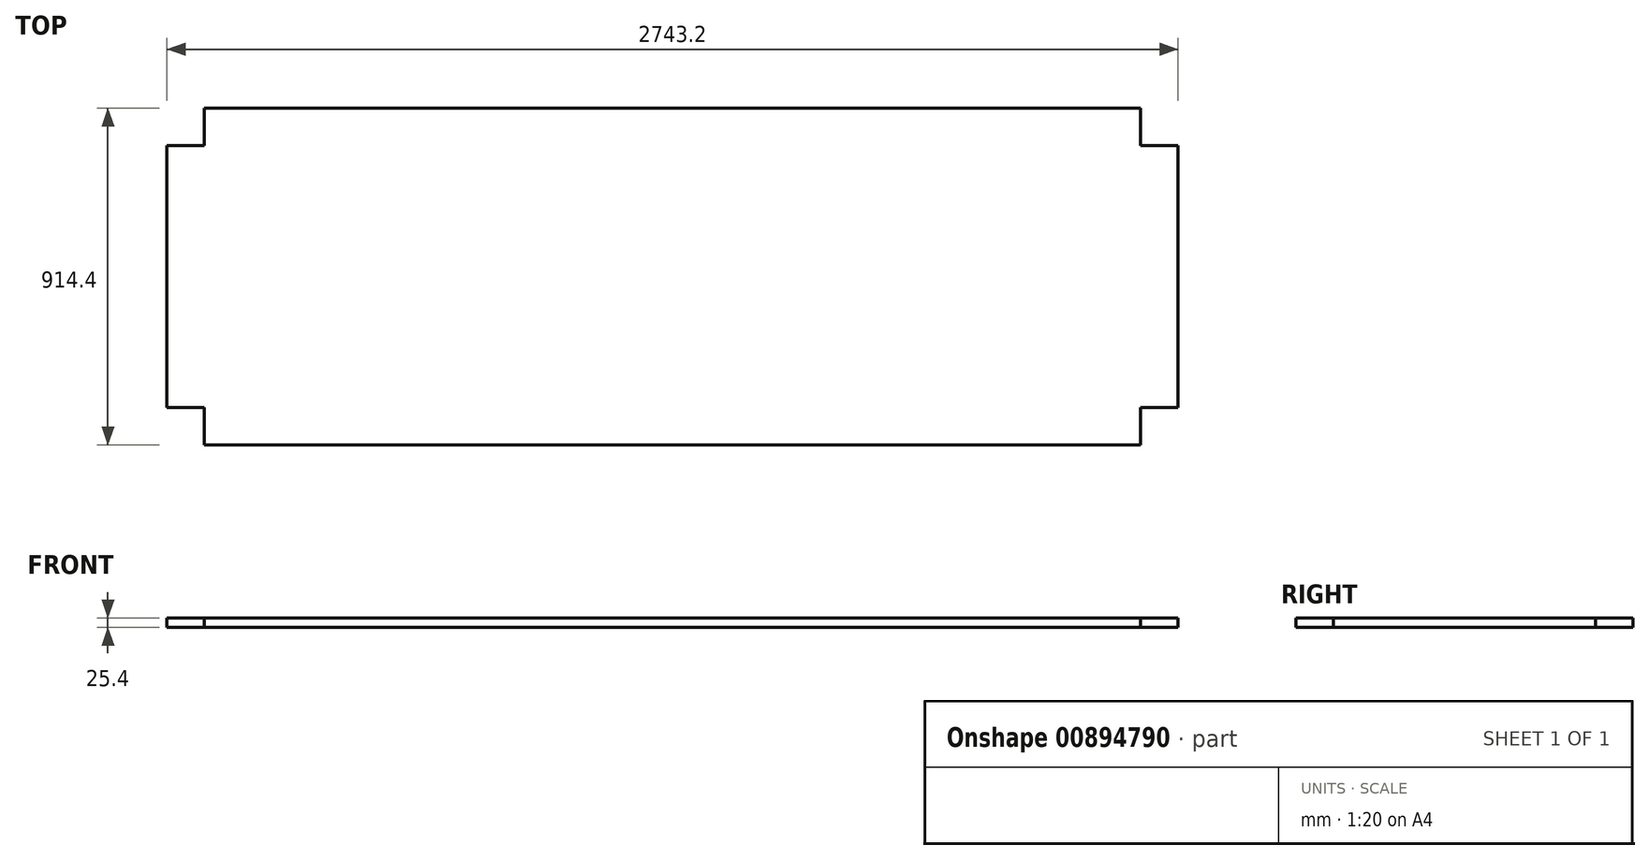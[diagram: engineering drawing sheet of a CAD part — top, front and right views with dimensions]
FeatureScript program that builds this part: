
annotation { "Feature Type Name" : "Feature", "Feature Type Description" : "" }
export const myFeature = defineFeature(function(context is Context, id is Id, definition is map)
    precondition{}
    {
        {
            var Q0;
            Q0=qCreatedBy(makeId("Top.planeOp"),FACE);
            var sketch = newSketch(context, id + "F0", { "sketchPlane" : qUnion([Q0])});
            skLineSegment(sketch, "E0", {"start": v(0, 101.6) * mm, "end": v(0, 812.8) * mm});
            skLineSegment(sketch, "E1", {"start": v(0, 812.8) * mm, "end": v(101.6, 812.8) * mm});
            skLineSegment(sketch, "E2", {"start": v(101.6, 812.8) * mm, "end": v(101.6, 914.4) * mm});
            skLineSegment(sketch, "E3", {"start": v(101.6, 914.4) * mm, "end": v(2641.6, 914.4) * mm});
            skLineSegment(sketch, "E4", {"start": v(2641.6, 914.4) * mm, "end": v(2641.6, 812.8) * mm});
            skLineSegment(sketch, "E5", {"start": v(2641.6, 812.8) * mm, "end": v(2743.2, 812.8) * mm});
            skLineSegment(sketch, "E6", {"start": v(2743.2, 812.8) * mm, "end": v(2743.2, 101.6) * mm});
            skLineSegment(sketch, "E7", {"start": v(2743.2, 101.6) * mm, "end": v(2641.6, 101.6) * mm});
            skLineSegment(sketch, "E8", {"start": v(2641.6, 101.6) * mm, "end": v(2641.6, 0) * mm});
            skLineSegment(sketch, "E9", {"start": v(2641.6, 0) * mm, "end": v(101.6, 0) * mm});
            skLineSegment(sketch, "E10", {"start": v(101.6, 0) * mm, "end": v(101.6, 101.6) * mm});
            skLineSegment(sketch, "E11", {"start": v(101.6, 101.6) * mm, "end": v(0, 101.6) * mm});
            skSolve(sketch);
        }
        {
            var Q0;
            Q0 = qSketchRegion(id + "F0", true);
            extrude(context, id + "F1", {"entities" : qUnion([Q0]), "depth" : 25.4 * mm, "offsetDistance" : 25.4 * mm});
        }
    });
